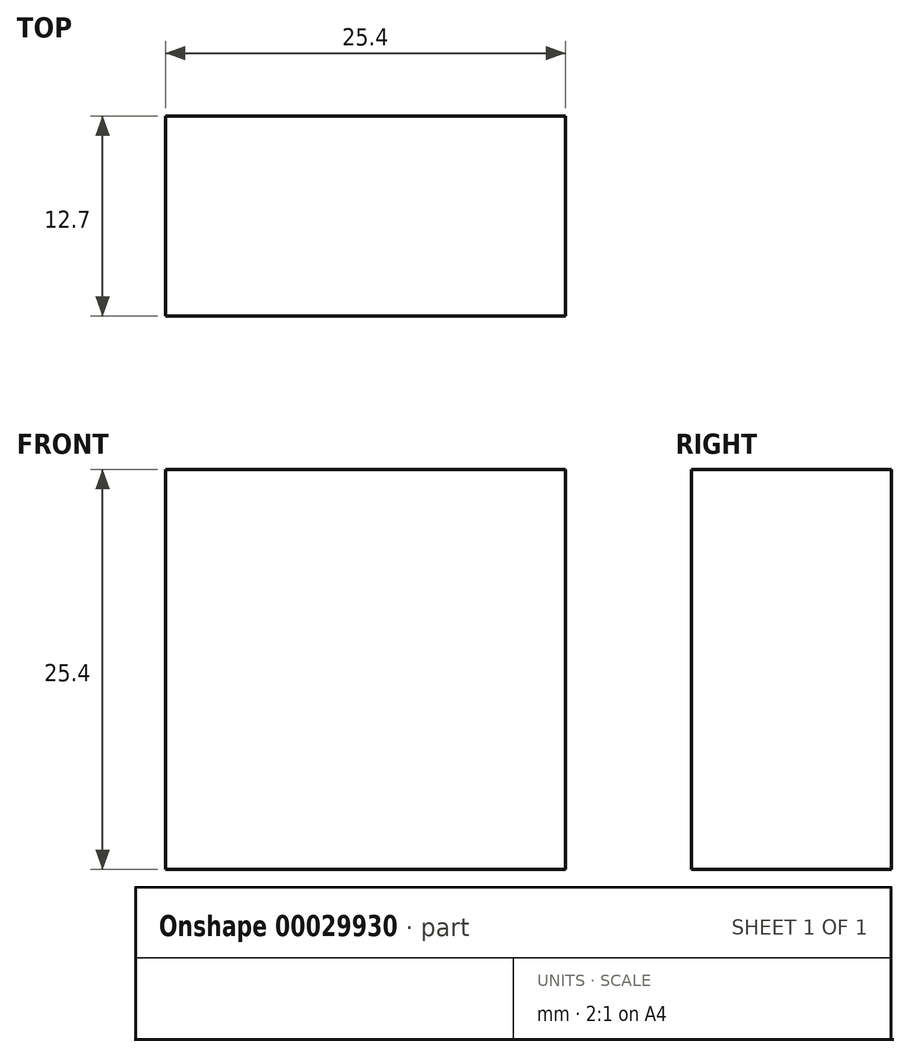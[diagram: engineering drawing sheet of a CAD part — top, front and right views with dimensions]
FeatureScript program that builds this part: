
annotation { "Feature Type Name" : "Feature", "Feature Type Description" : "" }
export const myFeature = defineFeature(function(context is Context, id is Id, definition is map)
    precondition{}
    {
        {
            var Q0;
            Q0=qCreatedBy(makeId("Front.planeOp"),FACE);
            var sketch = newSketch(context, id + "F0", { "sketchPlane" : qUnion([Q0])});
            skLineSegment(sketch, "E0.bottom", {"start": v(-29.59, 33.58) * mm, "end": v(-4.19, 33.58) * mm});
            skLineSegment(sketch, "E0.top", {"start": v(-29.59, 8.18) * mm, "end": v(-4.19, 8.18) * mm});
            skLineSegment(sketch, "E0.left", {"start": v(-29.59, 33.58) * mm, "end": v(-29.59, 8.18) * mm});
            skLineSegment(sketch, "E0.right", {"start": v(-4.19, 33.58) * mm, "end": v(-4.19, 8.18) * mm});
            skSolve(sketch);
        }
        {
            var Q0;
            Q0=makeQuery(id+"F0.imprint","IMPRINT",FACE,{"disambiguationData":[TD([[makeQuery(id+"F0.imprint","IMPRINT",EDGE,{"derivedFrom":sQuery(id+"F0.wireOp",EDGE,"E0.bottom")}),-1.0]])]});
            extrude(context, id + "F1", {"entities" : qUnion([Q0]), "depth" : 12.7 * mm});
        }
    });
